# Revit family: LWFLED-2IPREM-XX_Non-Hosted_R16
name_source: partatom
category: Lighting Fixtures
revit_build: Autodesk Revit 2016 (Build: 20151007_0715(x64)
units: mm (PartAtom-declared; Revit-internal decimal feet)

## family parameters
Always vertical = Yes
Cut with Voids When Loaded = No
Light Source = Yes
OmniClass Number = 23.80.70.00
OmniClass Title = Lighting
Part Type = Normal
Room Calculation Point = No
Round Connector Dimension = Use Diameter
Shared = No
Work Plane-Based = No

## types (2) — shared parameters
AS2293 Classification = C0=N/A C90=N/A
Battery = 6.6V 2500mAh
Battery Type = L10 Lithium Nanophosphate
Charger Method = Intelligent current limited constant voltage
Color Filter = 16777215
Construction = Polycarbonate
Dimension LED Enclosure (LxWxH) = 80mm x 82mm x 66mm
Dimensions Main Enclosure (LxWxH) = 380mm x 180mm x 130mm
Dimming Lamp Color Temperature Shift = <None>
Emit Shape Visible in Rendering = No
Emit from Circle Diameter = 610 mm
IK Rating = IK08
IP Rating = IP65
Lamp = 2 x LED Heads (adjustable)
Manufacturer = Clevertronics
Mounting = Surface mount
Operating Mode = Non-maintained
Operating Voltage = 240V AC; 50Hz
Photometric Web File = ll19822 - LWFLED-ZW.IES
Power Consumption = 1.0 Watts (Standby), 5.4 Watts (Max)
Product Description = Weatherproof Supalite flood unit
Replacement Battery = 1530190 BATT:L10. 6.6V 2.5Ah..2m lead.Stck.Brkt.
Replacement Driver = LCPLED-WP-18V500CCKIT LED Power Pack, 18V 500mA, IP Loom, L10
Replacement Lamp = 1100550 WP Led Head, c/w Led's & Loom
Testing System = Clevertest Plus Enabled (Not activated by default)
Tilt Angle = 90.00°
Total Lumen Output = 495lm per lamp head
Weight - Head = 0.36Kg
Weight - Main Enclosure = 2.6kg

## per-type parameters (varying)
| type | Description | Operating Temperature |
| LWFLED-2IPREM | WP Led Supalite EmgFlood,NM, REM,L10,CTP | -40˚C to 40˚C |
| LWFLED-2IPREM-BLK | WP Led Supalite Emg Flood,NM,REM,L10,CTP | 0˚C to 40˚C |

note: column(s) folded — value = type name in every type: MIC Number, Model

## geometry (parser evidence)
native form markers: Sweep x6
no freeform markers — native parametric forms only
